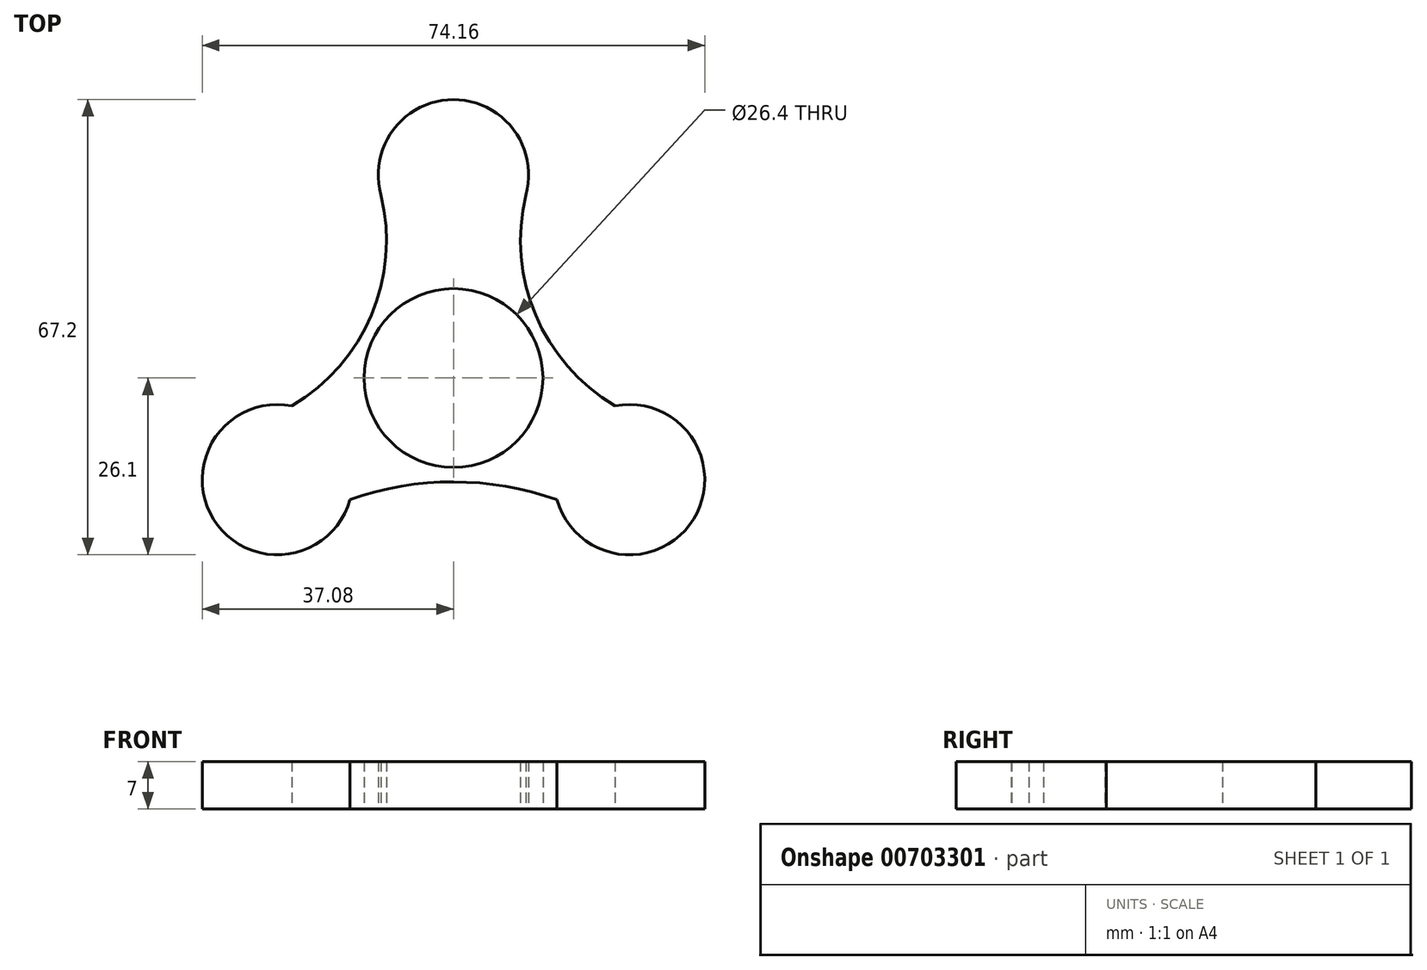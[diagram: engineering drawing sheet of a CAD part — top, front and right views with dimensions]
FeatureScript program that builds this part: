
annotation { "Feature Type Name" : "Feature", "Feature Type Description" : "" }
export const myFeature = defineFeature(function(context is Context, id is Id, definition is map)
    precondition{}
    {
        {
            var Q0;
            Q0=qCreatedBy(makeId("Top.planeOp"),FACE);
            var sketch = newSketch(context, id + "F0", { "sketchPlane" : qUnion([Q0])});
            skCircle(sketch, "E0", {"center": v(0, 0) * mm, "radius": 11.89 * mm});
            skSolve(sketch);
        }
        {
            var Q0;
            Q0=qCreatedBy(makeId("Top.planeOp"),FACE);
            var sketch = newSketch(context, id + "F1", { "sketchPlane" : qUnion([Q0])});
            skArc(sketch, "E1", {"start": v(10.7, 27.03) * mm, "mid": v(0, 41.1) * mm, "end": v(-10.7, 27.03) * mm});
            skArc(sketch, "E2.1.0", {"start": v(-23.83, -4.11) * mm, "mid": v(-35.42, -20.85) * mm, "end": v(-15.27, -17.92) * mm});
            skArc(sketch, "E2.2.0", {"start": v(15.28, -17.96) * mm, "mid": v(35.43, -20.83) * mm, "end": v(23.83, -4.11) * mm});
            skPoint(sketch, "E2.center", {"position": v(0, 0) * mm});
            skCircle(sketch, "E3", {"center": v(0, 0) * mm, "radius": 13.2 * mm});
            skArc(sketch, "E4", {"start": v(-23.83, -4.11) * mm, "mid": v(-12.02, 9.53) * mm, "end": v(-10.82, 27.53) * mm});
            skArc(sketch, "E5.MirrorCS", {"start": v(23.83, -4.11) * mm, "mid": v(12.02, 9.53) * mm, "end": v(10.82, 27.53) * mm});
            skArc(sketch, "E6", {"start": v(15.28, -17.96) * mm, "mid": v(0, -15.34) * mm, "end": v(-15.27, -17.92) * mm});
            skSolve(sketch);
        }
        {
            var Q0;
            Q0 = qSketchRegion(id + "F1", true);
            extrude(context, id + "F2", {"entities" : qUnion([Q0]), "depth" : 7 * mm, "offsetDistance" : 25 * mm});
        }
    });
